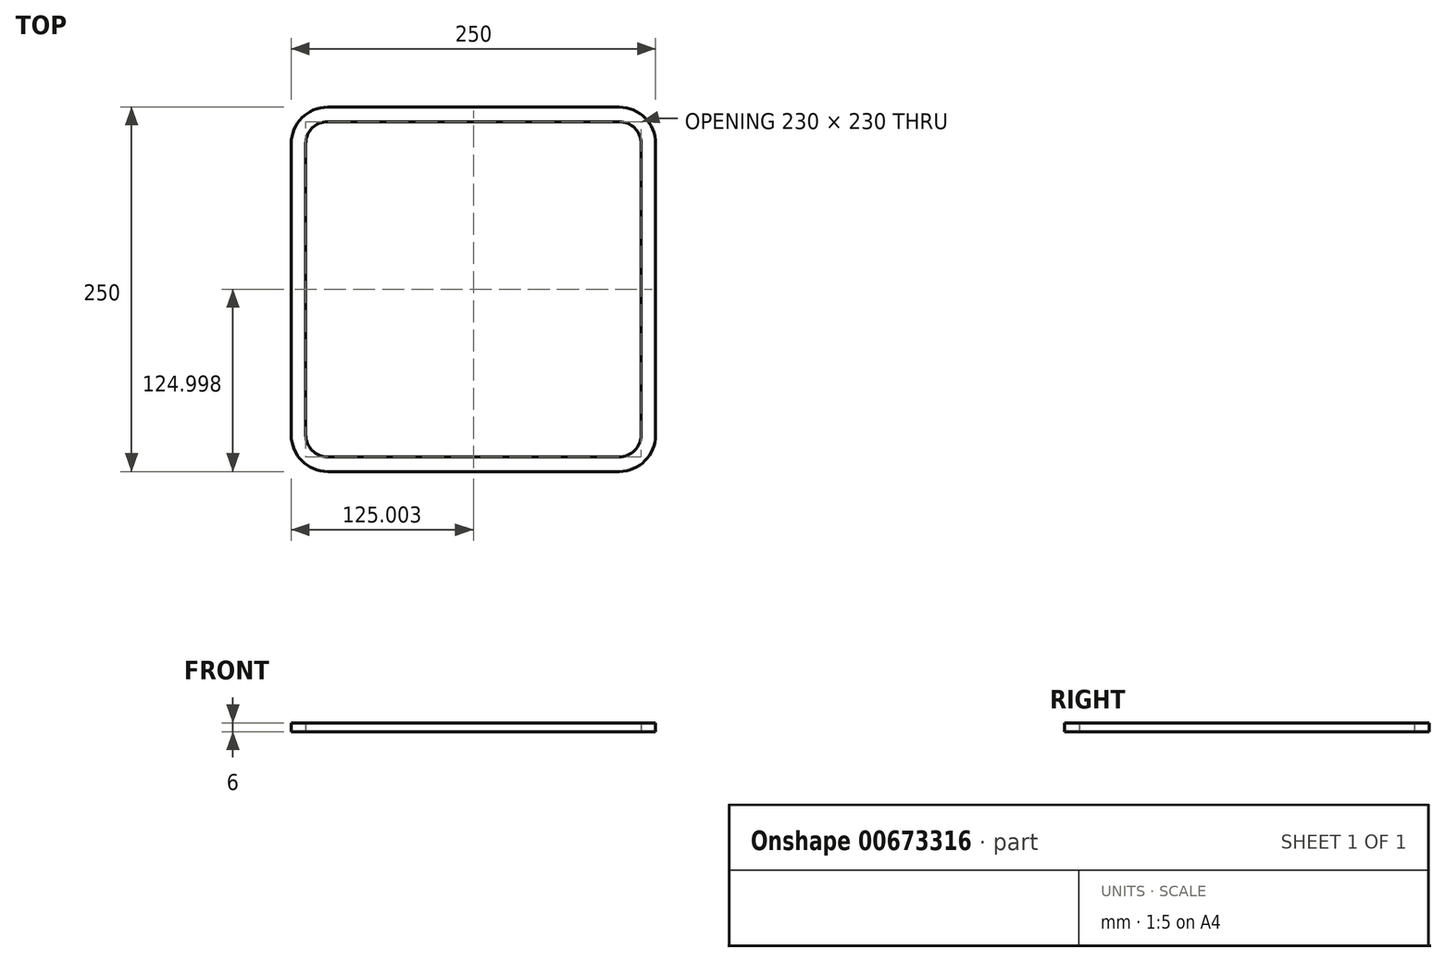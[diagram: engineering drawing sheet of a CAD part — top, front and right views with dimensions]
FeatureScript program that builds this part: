
annotation { "Feature Type Name" : "Feature", "Feature Type Description" : "" }
export const myFeature = defineFeature(function(context is Context, id is Id, definition is map)
    precondition{}
    {
        {
            var Q0;
            Q0=qCreatedBy(makeId("Top.planeOp"),FACE);
            var sketch = newSketch(context, id + "F0", { "sketchPlane" : qUnion([Q0])});
            skLineSegment(sketch, "E0.bottom", {"start": v(-145.55, 137.8) * mm, "end": v(54.45, 137.8) * mm});
            skLineSegment(sketch, "E0.top", {"start": v(-145.55, -112.2) * mm, "end": v(54.45, -112.2) * mm});
            skLineSegment(sketch, "E0.left", {"start": v(-170.55, 112.8) * mm, "end": v(-170.55, -87.2) * mm});
            skLineSegment(sketch, "E0.right", {"start": v(79.45, 112.8) * mm, "end": v(79.45, -87.2) * mm});
            skPoint(sketch, "E1.visualSharp", {"position": v(-170.55, 137.8) * mm});
            skArc(sketch, "E1.filletArc", {"start": v(-145.55, 137.8) * mm, "mid": v(-163.22, 130.48) * mm, "end": v(-170.55, 112.8) * mm});
            skPoint(sketch, "E2.visualSharp", {"position": v(79.45, 137.8) * mm});
            skArc(sketch, "E2.filletArc", {"start": v(79.45, 112.8) * mm, "mid": v(72.13, 130.48) * mm, "end": v(54.45, 137.8) * mm});
            skPoint(sketch, "E3.visualSharp", {"position": v(79.45, -112.2) * mm});
            skArc(sketch, "E3.filletArc", {"start": v(54.45, -112.2) * mm, "mid": v(72.13, -104.88) * mm, "end": v(79.45, -87.2) * mm});
            skPoint(sketch, "E4.visualSharp", {"position": v(-170.55, -112.2) * mm});
            skArc(sketch, "E4.filletArc", {"start": v(-170.55, -87.2) * mm, "mid": v(-163.22, -104.88) * mm, "end": v(-145.55, -112.2) * mm});
            skArc(sketch, "E5.0", {"start": v(-145.55, 127.8) * mm, "mid": v(-156.15, 123.4) * mm, "end": v(-160.55, 112.8) * mm});
            skLineSegment(sketch, "E5.1", {"start": v(-160.55, 112.8) * mm, "end": v(-160.55, -87.2) * mm});
            skLineSegment(sketch, "E5.2", {"start": v(-145.55, 127.8) * mm, "end": v(54.45, 127.8) * mm});
            skArc(sketch, "E5.3", {"start": v(-160.55, -87.2) * mm, "mid": v(-156.15, -97.8) * mm, "end": v(-145.55, -102.2) * mm});
            skArc(sketch, "E5.4", {"start": v(69.45, 112.8) * mm, "mid": v(65.06, 123.4) * mm, "end": v(54.45, 127.8) * mm});
            skLineSegment(sketch, "E5.5", {"start": v(69.45, 112.8) * mm, "end": v(69.45, -87.2) * mm});
            skArc(sketch, "E5.6", {"start": v(54.45, -102.2) * mm, "mid": v(65.06, -97.8) * mm, "end": v(69.45, -87.2) * mm});
            skLineSegment(sketch, "E5.7", {"start": v(-145.55, -102.2) * mm, "end": v(54.45, -102.2) * mm});
            skSolve(sketch);
        }
        {
            var Q0;
            Q0=makeQuery(id+"F0.imprint","IMPRINT",FACE,{"disambiguationData":[TD([[makeQuery(id+"F0.imprint","IMPRINT",EDGE,{"derivedFrom":sQuery(id+"F0.wireOp",EDGE,"E0.bottom")}),-1.0]])]});
            extrude(context, id + "F1", {"entities" : qUnion([Q0]), "depth" : 6 * mm, "offsetDistance" : 25 * mm});
        }
    });
